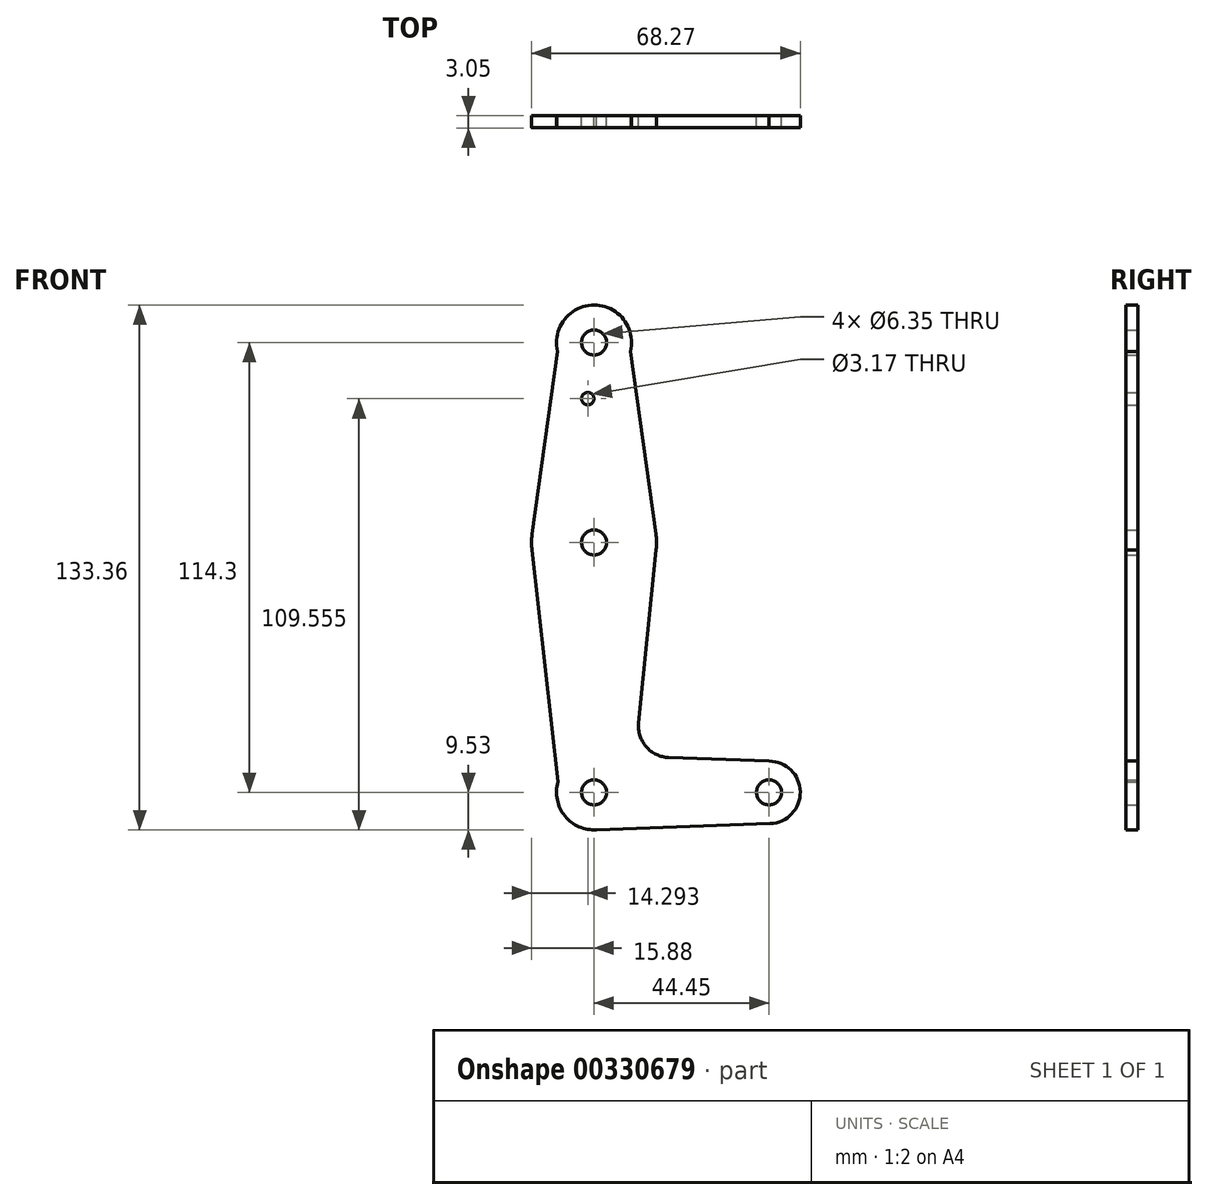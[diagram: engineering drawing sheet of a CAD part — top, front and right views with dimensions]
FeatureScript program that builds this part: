
annotation { "Feature Type Name" : "Feature", "Feature Type Description" : "" }
export const myFeature = defineFeature(function(context is Context, id is Id, definition is map)
    precondition{}
    {
        {
            var Q0;
            Q0=qCreatedBy(makeId("Front.planeOp"),FACE);
            var sketch = newSketch(context, id + "F0", { "sketchPlane" : qUnion([Q0])});
            skCircle(sketch, "E0", {"center": v(0, 114.3) * mm, "radius": 9.53 * mm});
            skCircle(sketch, "E1", {"center": v(0, 63.5) * mm, "radius": 15.88 * mm});
            skCircle(sketch, "E2", {"center": v(0, 0) * mm, "radius": 9.53 * mm});
            skCircle(sketch, "E3", {"center": v(44.45, 0) * mm, "radius": 7.94 * mm});
            skCircle(sketch, "E4", {"center": v(0, 63.5) * mm, "radius": 3.17 * mm});
            skCircle(sketch, "E5", {"center": v(0, 114.3) * mm, "radius": 3.17 * mm});
            skCircle(sketch, "E6", {"center": v(0, 0) * mm, "radius": 3.17 * mm});
            skCircle(sketch, "E7", {"center": v(44.45, 0) * mm, "radius": 3.17 * mm});
            skLineSegment(sketch, "E8", {"start": v(0, 0) * mm, "end": v(0, 114.3) * mm});
            skLineSegment(sketch, "E9", {"start": v(0, 0) * mm, "end": v(44.45, 0) * mm});
            skLineSegment(sketch, "E10", {"start": v(-9.26, 112.06) * mm, "end": v(-15.72, 65.7) * mm});
            skLineSegment(sketch, "E11", {"start": v(-15.76, 61.61) * mm, "end": v(-9.15, 2.64) * mm});
            skLineSegment(sketch, "E12", {"start": v(9.26, 112.06) * mm, "end": v(15.72, 65.7) * mm});
            skLineSegment(sketch, "E13", {"start": v(15.76, 61.61) * mm, "end": v(11.34, 17.59) * mm});
            skLineSegment(sketch, "E14", {"start": v(18.97, 8.85) * mm, "end": v(44.45, 7.94) * mm});
            skLineSegment(sketch, "E15", {"start": v(0, -9.53) * mm, "end": v(44.73, -7.93) * mm});
            skArc(sketch, "E16.filletArc", {"start": v(11.34, 17.59) * mm, "mid": v(13.26, 11.57) * mm, "end": v(18.97, 8.85) * mm});
            skCircle(sketch, "E17", {"center": v(-1.59, 100.03) * mm, "radius": 1.59 * mm});
            skSolve(sketch);
        }
        {
            var Q0;
            Q0 = qSketchRegion(id + "F0", true);
            var Q1;
            {var subQ0=sQuery(id+"F0.wireOp",EDGE,"E8");var subQ1=sQuery(id+"F0.wireOp",EDGE,"E2");var subQ2=makeQuery(id+"F0.imprint","INTERSECT",VERTEX,{"derivedFrom":[subQ1,subQ0]});Q1=makeQuery(id+"F0.imprint","IMPRINT",FACE,{"disambiguationData":[TD([[makeQuery(id+"F0.imprint","IMPRINT",EDGE,{"disambiguationData":[TD([[subQ2,1.0]])],"derivedFrom":subQ1}),1.0]])]});}
            extrude(context, id + "F1", {"entities" : qUnion([Q0, Q1]), "depth" : 3.05 * mm});
        }
    });
